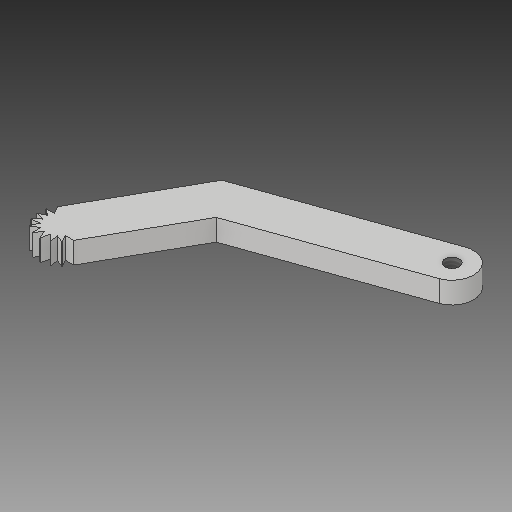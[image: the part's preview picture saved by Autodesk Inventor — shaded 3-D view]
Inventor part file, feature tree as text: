
AUTODESK INVENTOR PART (.ipt)
format: ipt  version: 2017 (Build 210142000, 142)  size: 146,432 bytes
history: native  units: mm
features: sketch x3, extrude x2, hole x1
ambient origin geometry x8: Origin, YZ Plane, XZ Plane, XY Plane, X Axis, Y Axis, Z Axis, Center Point
bodies: Solid1 (feature_tree)
feature tree (6):
  extrude  "Extrusion1"  Depth=5.0mm
  hole  "Hole1"  [1 undecoded]
  extrude  "Extrusion2"  Depth=5.0mm
  sketch  "Sketch1"  dims[d0=5.0mm d1=5.0mm]
  sketch  "Sketch2"  dims[d2=40.707766mm d3=5.0mm]
  sketch  "Sketch3"  dims[d4=25.384678mm d5=29.129655mm d6=53.5mm d7=5.0mm d8=0.0mm d9=3.302mm d10=8.331mm d11=4.0mm d12=2.0mm d13=90.0deg d14=12.3mm d15=20.594885mm d16=2.0mm d17=90.0mm d19=180.0deg d21=5.0mm d22=0.0mm]
note: 1 required parameter value undecoded (feature->parameter linkage not recoverable at this tier; creation-order binding heuristic only, values carry confidence <= 0.55)
